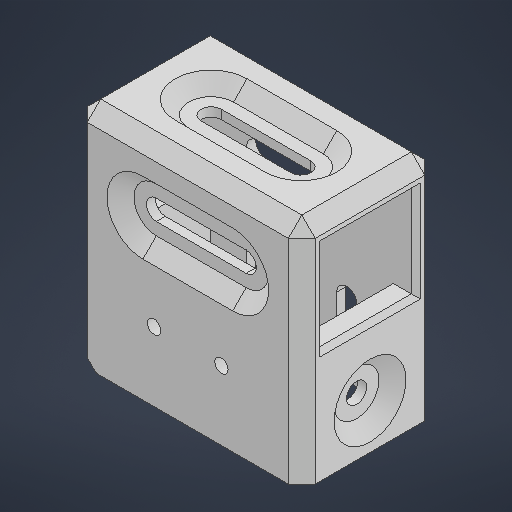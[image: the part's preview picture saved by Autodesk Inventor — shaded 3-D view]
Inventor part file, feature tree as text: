
AUTODESK INVENTOR PART (.ipt)
format: ipt  version: 2025.1 (Build 291241000, 241)  size: 763,392 bytes
history: native  units: mm
features: extrude x12, sketch x6, projected_geometry x5, chamfer x3, pattern_circular x1
ambient origin geometry x8: Origin, YZ Plane, XZ Plane, XY Plane, X Axis, Y Axis, Z Axis, Center Point
bodies: Solid1 (feature_tree)
feature tree (27):
  sketch  "Sketch1"  dims[d0=20.4mm d1=20.4mm]
  extrude  "Extrusion1"  Depth=20.4mm
  sketch  "Sketch2"  dims[d2=5.0mm d3=40.8mm d4=0.0mm]
  extrude  "Extrusion2"  Depth=40.8mm TaperAngle=0.0deg
  extrude  "Extrusion3"  Depth=20.0mm
  pattern_circular  "Circular Pattern1"  Count=4  [1 undecoded]
  sketch  "Sketch3"  dims[d5=4.5mm d7=20.0mm]
  extrude  "Extrusion4"  Depth=3.0mm TaperAngle=180.0deg
  extrude  "Extrusion5"  Depth=3.0mm
  sketch  "Sketch4"  dims[d8=10.0mm d9=40.0mm d10=0.0mm]
  extrude  "Extrusion6"  Depth=3.0mm
  extrude  "Extrusion11"  Depth=3.0mm TaperAngle=0.0deg
  extrude  "Extrusion7"  Depth=3.0mm TaperAngle=0.0deg
  extrude  "Extrusion8"  Depth=10.0mm
  sketch  "Sketch5"  dims[d11=3.0mm d12=0.0mm d13=30.0mm d14=180.0deg]
  extrude  "Extrusion9"  Depth=3.0mm
  extrude  "Extrusion10"  Depth=10.0mm
  extrude  "Extrusion12"  Depth=10.0mm TaperAngle=0.0deg
  chamfer  "Chamfer3"  Distance=10.0mm
  chamfer  "Chamfer2"  Distance=10.0mm
  chamfer  "Chamfer4"  Distance=10.0mm
  projected_geometry  "Projected Loop1"
  projected_geometry  "Projected Loop2"
  projected_geometry  "Projected Loop3"
  sketch  "Sketch6"  dims[d16=40.8mm d17=20.4mm d18=5.0mm d19=20.0mm d20=0.0mm d21=40.0mm d22=0.0mm d23=10.0mm d24=4.5mm d25=10.0mm d26=10.0mm d27=0.0mm d31=10.0mm d32=0.0mm d33=10.0mm d34=0.0mm d35=10.0mm d37=4.5mm d38=8.0mm d39=10.0mm d40=10.0mm d41=10.0mm d42=0.0mm d43=3.0mm d44=0.0mm d45=3.0mm d46=0.0mm d47=1.0mm d48=2.0mm d49=45.0deg d50=3.0mm d51=15.0mm d53=0.0mm d54=0.0mm d55=5.0mm d56=2.0mm d57=45.0deg d58=20.0mm d59=3.0mm d60=2.0mm d61=45.0deg]
  projected_geometry  "Projected Loop4"
  projected_geometry  "Projected Loop5"
note: 1 required parameter value undecoded (feature->parameter linkage not recoverable at this tier; creation-order binding heuristic only, values carry confidence <= 0.55)
